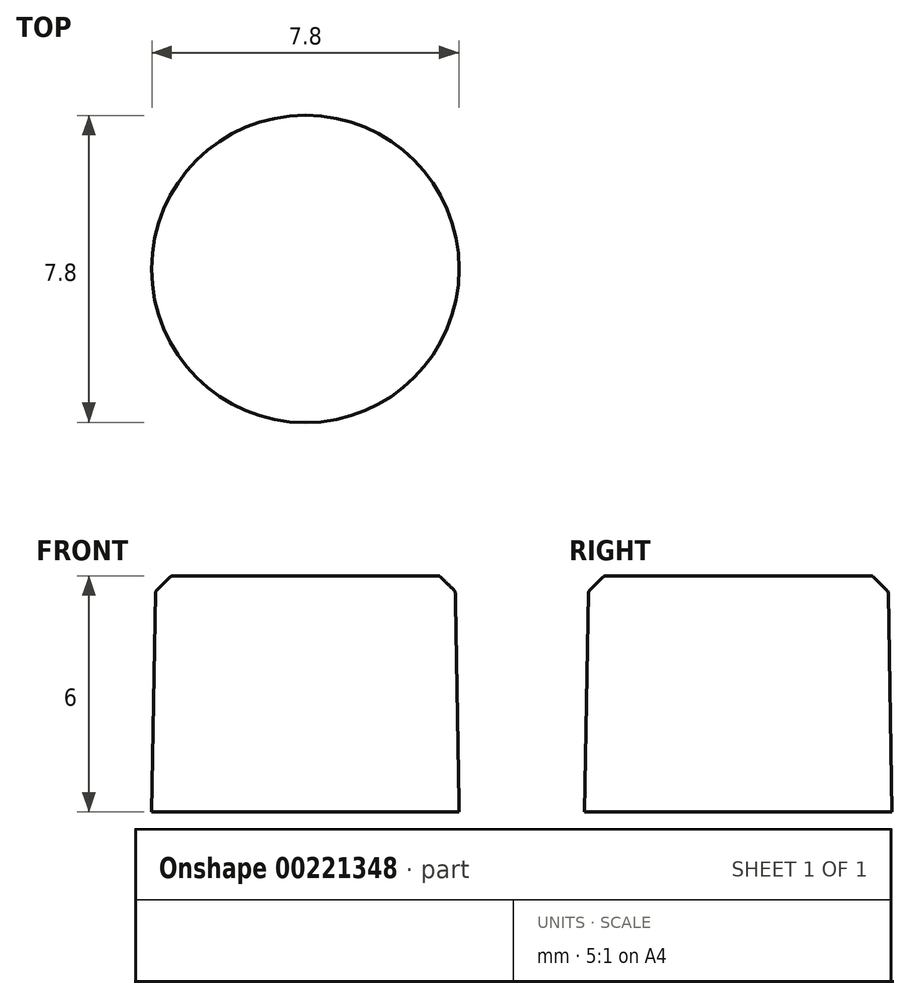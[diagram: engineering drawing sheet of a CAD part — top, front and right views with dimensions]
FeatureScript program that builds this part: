
annotation { "Feature Type Name" : "Feature", "Feature Type Description" : "" }
export const myFeature = defineFeature(function(context is Context, id is Id, definition is map)
    precondition{}
    {
        {
            var Q0;
            Q0=qCreatedBy(makeId("Top.planeOp"),FACE);
            var sketch = newSketch(context, id + "F0", { "sketchPlane" : qUnion([Q0])});
            skCircle(sketch, "E0", {"center": v(0, 0) * mm, "radius": 4 * mm});
            skSolve(sketch);
        }
        {
            var Q0;
            Q0 = qSketchRegion(id + "F0", true);
            extrude(context, id + "F1", {"entities" : qUnion([Q0]), "depth" : 6 * mm});
        }
        {
            var Q0;
            Q0=makeQuery(id+"F1.opExtrude","CAP_EDGE",EDGE,{"disambiguationData":[OSD([sQuery(id+"F0.wireOp",EDGE,"E0")])],"isStart":false});
            chamfer(context, id + "F2", {"entities" : qUnion([Q0]), "chamferType" : ChamferType.OFFSET_ANGLE, "width" : .2 * mm, "oppositeDirection" : false, "angle" : 89 * degree, "tangentPropagation" : true});
        }
        {
            var Q0;
            {var subQ0=sQuery(id+"F0.wireOp",EDGE,"E0");Q0=makeQuery(id+"F2.opChamfer","BLEND_EDGE",EDGE,{"blendedFrom":[makeQuery(id+"F1.opExtrude","CAP_EDGE",EDGE,{"disambiguationData":[OSD([subQ0])],"isStart":false}),makeQuery(id+"F1.opExtrude","CAP_FACE",FACE,{"disambiguationData":[OSD([subQ0])],"isStart":false})],"blendedInto":[makeQuery(id+"F1.opExtrude","CAP_FACE",FACE,{"disambiguationData":[OSD([subQ0])],"isStart":false})]});}
            chamfer(context, id + "F3", {"entities" : qUnion([Q0]), "width" : .4 * mm, "tangentPropagation" : true});
        }
        {
            var Q0;
            {var subQ0=sQuery(id+"F0.wireOp",EDGE,"E0");var subQ1=makeQuery(id+"F1.opExtrude","CAP_FACE",FACE,{"disambiguationData":[OSD([subQ0])],"isStart":false});Q0=makeQuery(id+"F3.opChamfer","BLEND_EDGE",EDGE,{"blendedFrom":[makeQuery(id+"F2.opChamfer","BLEND_EDGE",EDGE,{"blendedFrom":[makeQuery(id+"F1.opExtrude","CAP_EDGE",EDGE,{"disambiguationData":[OSD([subQ0])],"isStart":false}),subQ1],"blendedInto":[subQ1]}),subQ1],"blendedInto":[subQ1]});}
            var Q1;
            {var subQ0=sQuery(id+"F0.wireOp",EDGE,"E0");Q1=makeQuery(id+"F3.opChamfer","BLEND_EDGE",EDGE,{"blendedFrom":[makeQuery(id+"F2.opChamfer","BLEND_EDGE",EDGE,{"blendedFrom":[makeQuery(id+"F1.opExtrude","CAP_EDGE",EDGE,{"disambiguationData":[OSD([subQ0])],"isStart":false}),makeQuery(id+"F1.opExtrude","CAP_FACE",FACE,{"disambiguationData":[OSD([subQ0])],"isStart":false})],"blendedInto":[makeQuery(id+"F1.opExtrude","CAP_FACE",FACE,{"disambiguationData":[OSD([subQ0])],"isStart":false})]}),makeQuery(id+"F2.opChamfer","BLEND_FACE",FACE,{"disambiguationData":[OSD([subQ0])]})],"blendedInto":[makeQuery(id+"F2.opChamfer","BLEND_FACE",FACE,{"disambiguationData":[OSD([subQ0])]})]});}
            fillet(context, id + "F4", {"entities" : qUnion([Q0, Q1]), "radius" : .1 * mm, "tangentPropagation" : true, "allowEdgeOverflow" : false});
        }
    });
